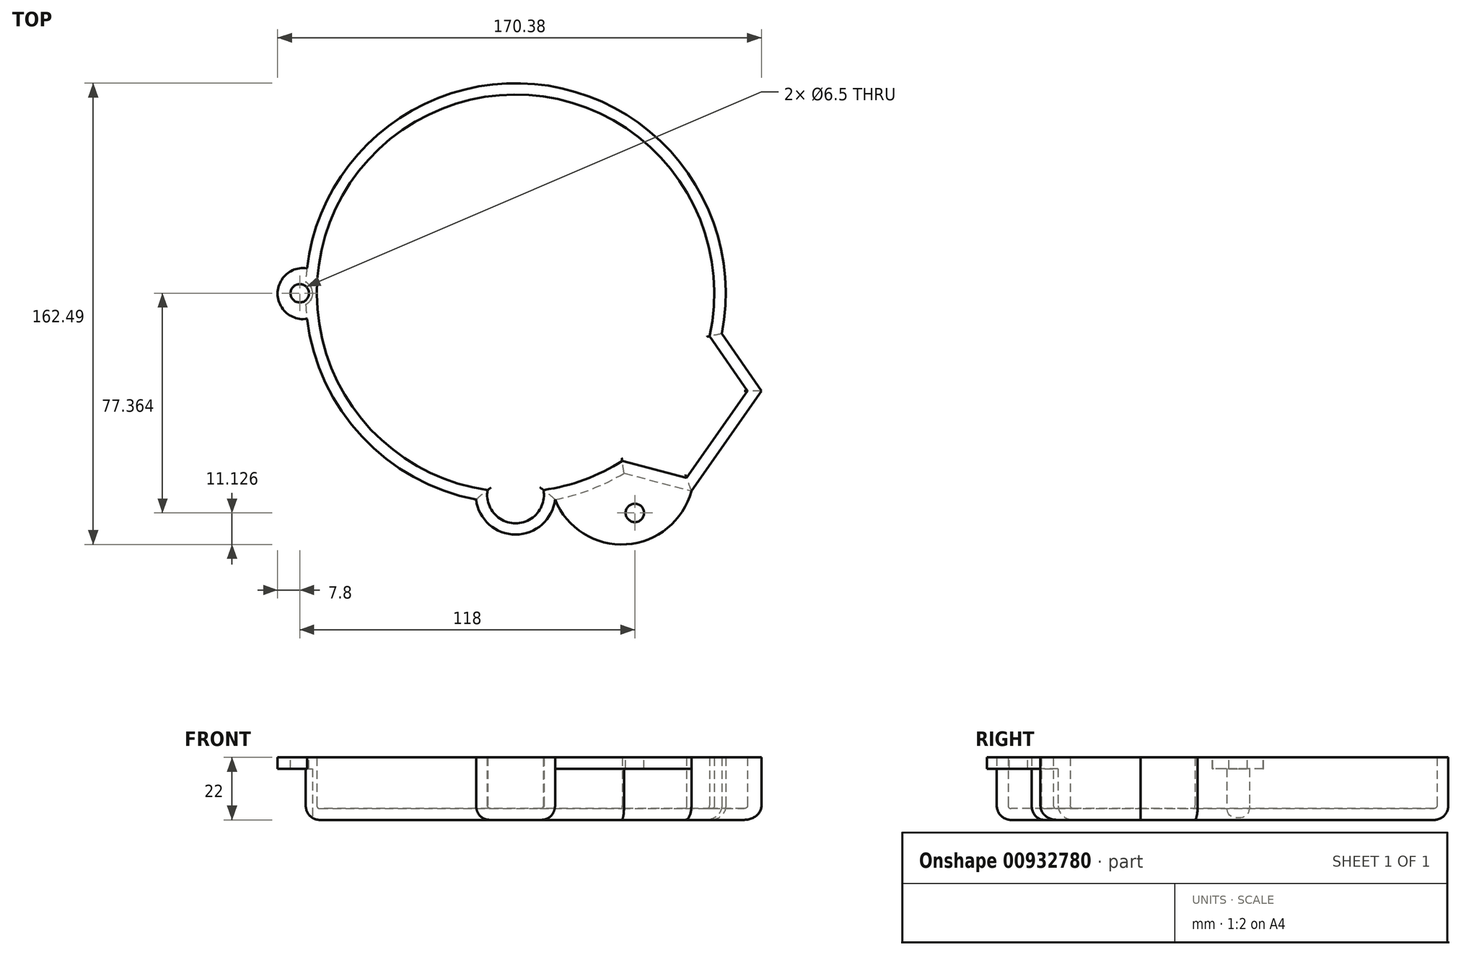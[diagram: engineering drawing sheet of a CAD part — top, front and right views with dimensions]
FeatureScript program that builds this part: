
annotation { "Feature Type Name" : "Feature", "Feature Type Description" : "" }
export const myFeature = defineFeature(function(context is Context, id is Id, definition is map)
    precondition{}
    {
        {
            var Q0;
            Q0=qCreatedBy(makeId("Top.planeOp"),FACE);
            var sketch = newSketch(context, id + "F0", { "sketchPlane" : qUnion([Q0])});
            skCircle(sketch, "E0", {"center": v(0, 0) * mm, "radius": 74 * mm});
            skSolve(sketch);
        }
        {
            var Q0;
            Q0 = qSketchRegion(id + "F0", true);
            extrude(context, id + "F1", {"entities" : qUnion([Q0]), "depth" : 22 * mm, "offsetDistance" : 25 * mm});
        }
        {
            var Q0;
            Q0=makeQuery(id+"F1.opExtrude","CAP_FACE",FACE,{"disambiguationData":[OSD([sQuery(id+"F0.wireOp",EDGE,"E0")])],"isStart":true});
            var sketch = newSketch(context, id + "F2", { "sketchPlane" : qUnion([Q0])});
            skCircle(sketch, "E1", {"center": v(0, 71) * mm, "radius": 14 * mm});
            skSolve(sketch);
        }
        {
            var Q0;
            Q0 = qSketchRegion(id + "F2", true);
            extrude(context, id + "F3", {"entities" : qUnion([Q0]), "operationType" : NewBodyOperationType.ADD, "oppositeDirection" : true, "depth" : 22 * mm, "offsetDistance" : 25 * mm});
        }
        {
            var Q0;
            Q0=makeQuery(id+"F3.boolean.opBoolean","MERGE",FACE,{"derivedFrom":[makeQuery(id+"F1.opExtrude","CAP_FACE",FACE,{"disambiguationData":[OSD([sQuery(id+"F0.wireOp",EDGE,"E0")])],"isStart":true}),makeQuery(id+"F3.opExtrude","CAP_FACE",FACE,{"disambiguationData":[OSD([sQuery(id+"F2.wireOp",EDGE,"E1")])],"isStart":true})]});
            var sketch = newSketch(context, id + "F4", { "sketchPlane" : qUnion([Q0])});
            skLineSegment(sketch, "E2", {"start": v(38.19, 63.38) * mm, "end": v(61.9, 69.62) * mm});
            skLineSegment(sketch, "E3", {"start": v(61.9, 69.62) * mm, "end": v(86.58, 34.4) * mm});
            skLineSegment(sketch, "E4", {"start": v(86.58, 34.4) * mm, "end": v(72.62, 14.24) * mm});
            skLineSegment(sketch, "E5", {"start": v(38.19, 63.38) * mm, "end": v(72.62, 14.24) * mm});
            skSolve(sketch);
        }
        {
            var Q0;
            Q0 = qSketchRegion(id + "F4", true);
            extrude(context, id + "F5", {"entities" : qUnion([Q0]), "operationType" : NewBodyOperationType.ADD, "oppositeDirection" : true, "depth" : 22 * mm, "offsetDistance" : 25 * mm});
        }
        {
            var Q0;
            {var subQ1=sQuery(id+"F0.wireOp",EDGE,"E0");var subQ2=sQuery(id+"F4.wireOp",EDGE,"E2");Q0=makeQuery(id+"F5.boolean.opBoolean","SPLIT",EDGE,{"disambiguationData":[TD([makeQuery(id+"F5.opExtrude","SWEPT_FACE",FACE,{"disambiguationData":[OSD([subQ2])]})])],"derivedFrom":makeQuery(id+"F1.opExtrude","CAP_EDGE",EDGE,{"disambiguationData":[OSD([subQ1])],"isStart":true})});}
            var Q1;
            Q1=makeQuery(id+"F5.opExtrude","CAP_EDGE",EDGE,{"disambiguationData":[OSD([sQuery(id+"F4.wireOp",EDGE,"E2")])],"isStart":true});
            var Q2;
            Q2=makeQuery(id+"F5.opExtrude","CAP_EDGE",EDGE,{"disambiguationData":[OSD([sQuery(id+"F4.wireOp",EDGE,"E3")])],"isStart":true});
            var Q3;
            Q3=makeQuery(id+"F5.opExtrude","CAP_EDGE",EDGE,{"disambiguationData":[OSD([sQuery(id+"F4.wireOp",EDGE,"E4")])],"isStart":true});
            var Q4;
            {var subQ1=sQuery(id+"F0.wireOp",EDGE,"E0");var subQ2=sQuery(id+"F4.wireOp",EDGE,"E4");Q4=makeQuery(id+"F5.boolean.opBoolean","SPLIT",EDGE,{"disambiguationData":[TD([makeQuery(id+"F5.opExtrude","SWEPT_FACE",FACE,{"disambiguationData":[OSD([subQ2])]})])],"derivedFrom":makeQuery(id+"F1.opExtrude","CAP_EDGE",EDGE,{"disambiguationData":[OSD([subQ1])],"isStart":true})});}
            var Q5;
            Q5=makeQuery(id+"F3.opExtrude","CAP_EDGE",EDGE,{"disambiguationData":[OSD([sQuery(id+"F2.wireOp",EDGE,"E1")])],"isStart":true});
            fillet(context, id + "F6", {"entities" : qUnion([Q0, Q1, Q2, Q3, Q4, Q5]), "radius" : 5 * mm, "tangentPropagation" : true, "allowEdgeOverflow" : false});
        }
        {
            var Q0;
            Q0=makeQuery(id+"F5.boolean.opBoolean","MERGE",FACE,{"derivedFrom":[makeQuery(id+"F3.boolean.opBoolean","MERGE",FACE,{"derivedFrom":[makeQuery(id+"F1.opExtrude","CAP_FACE",FACE,{"disambiguationData":[OSD([sQuery(id+"F0.wireOp",EDGE,"E0")])],"isStart":false}),makeQuery(id+"F3.opExtrude","CAP_FACE",FACE,{"disambiguationData":[OSD([sQuery(id+"F2.wireOp",EDGE,"E1")])],"isStart":false})]}),makeQuery(id+"F5.opExtrude","CAP_FACE",FACE,{"disambiguationData":[OSD([sQuery(id+"F4.wireOp",EDGE,"E2"),sQuery(id+"F4.wireOp",EDGE,"E3"),sQuery(id+"F4.wireOp",EDGE,"E4"),sQuery(id+"F4.wireOp",EDGE,"E5")])],"isStart":false})]});
            shell(context, id + "F7", {"entities" : qUnion([Q0]), "thickness" : 4 * mm});
        }
        {
            var Q0;
            Q0=makeQuery(id+"F5.boolean.opBoolean","MERGE",FACE,{"derivedFrom":[makeQuery(id+"F3.boolean.opBoolean","MERGE",FACE,{"derivedFrom":[makeQuery(id+"F1.opExtrude","CAP_FACE",FACE,{"disambiguationData":[OSD([sQuery(id+"F0.wireOp",EDGE,"E0")])],"isStart":false}),makeQuery(id+"F3.opExtrude","CAP_FACE",FACE,{"disambiguationData":[OSD([sQuery(id+"F2.wireOp",EDGE,"E1")])],"isStart":false})]}),makeQuery(id+"F5.opExtrude","CAP_FACE",FACE,{"disambiguationData":[OSD([sQuery(id+"F4.wireOp",EDGE,"E2"),sQuery(id+"F4.wireOp",EDGE,"E3"),sQuery(id+"F4.wireOp",EDGE,"E4"),sQuery(id+"F4.wireOp",EDGE,"E5")])],"isStart":false})]});
            var sketch = newSketch(context, id + "F8", { "sketchPlane" : qUnion([Q0])});
            skCircle(sketch, "E6", {"center": v(42, -77.36) * mm, "radius": 3.25 * mm});
            skArc(sketch, "E7", {"start": v(13.9, -72.68) * mm, "mid": v(39, -88.44) * mm, "end": v(61.9, -69.62) * mm});
            skLineSegment(sketch, "E8", {"start": v(61.9, -69.62) * mm, "end": v(37.39, -63.14) * mm});
            skLineSegment(sketch, "E9", {"start": v(13.9, -72.68) * mm, "end": v(37.39, -63.14) * mm});
            skSolve(sketch);
        }
        {
            var Q0;
            Q0 = qSketchRegion(id + "F8", true);
            extrude(context, id + "F9", {"entities" : qUnion([Q0]), "operationType" : NewBodyOperationType.ADD, "oppositeDirection" : true, "depth" : 4 * mm, "offsetDistance" : 25 * mm});
        }
        {
            var Q0;
            Q0=makeQuery(id+"F9.boolean.opBoolean","MERGE",FACE,{"derivedFrom":[makeQuery(id+"F5.boolean.opBoolean","MERGE",FACE,{"derivedFrom":[makeQuery(id+"F3.boolean.opBoolean","MERGE",FACE,{"derivedFrom":[makeQuery(id+"F1.opExtrude","CAP_FACE",FACE,{"disambiguationData":[OSD([sQuery(id+"F0.wireOp",EDGE,"E0")])],"isStart":false}),makeQuery(id+"F3.opExtrude","CAP_FACE",FACE,{"disambiguationData":[OSD([sQuery(id+"F2.wireOp",EDGE,"E1")])],"isStart":false})]}),makeQuery(id+"F5.opExtrude","CAP_FACE",FACE,{"disambiguationData":[OSD([sQuery(id+"F4.wireOp",EDGE,"E2"),sQuery(id+"F4.wireOp",EDGE,"E3"),sQuery(id+"F4.wireOp",EDGE,"E4"),sQuery(id+"F4.wireOp",EDGE,"E5")])],"isStart":false})]}),makeQuery(id+"F9.opExtrude","CAP_FACE",FACE,{"disambiguationData":[OSD([sQuery(id+"F8.wireOp",EDGE,"E6"),sQuery(id+"F8.wireOp",EDGE,"E7"),sQuery(id+"F8.wireOp",EDGE,"E8"),sQuery(id+"F8.wireOp",EDGE,"E9")])],"isStart":true})]});
            var sketch = newSketch(context, id + "F10", { "sketchPlane" : qUnion([Q0])});
            skCircle(sketch, "E10", {"center": v(-76, 0) * mm, "radius": 3.25 * mm});
            skArc(sketch, "E11", {"start": v(-73.48, 8.8) * mm, "mid": v(-83.8, -0.11) * mm, "end": v(-73.45, -9) * mm});
            skArc(sketch, "E12", {"start": v(-73.45, -9) * mm, "mid": v(-70.9, -0.1) * mm, "end": v(-73.48, 8.8) * mm});
            skSolve(sketch);
        }
        {
            var Q0;
            Q0 = qSketchRegion(id + "F10", true);
            extrude(context, id + "F11", {"entities" : qUnion([Q0]), "operationType" : NewBodyOperationType.ADD, "oppositeDirection" : true, "depth" : 4 * mm, "offsetDistance" : 25 * mm});
        }
        {
            var Q0;
            Q0=makeQuery(id+"F5.boolean.opBoolean","MERGE",FACE,{"derivedFrom":[makeQuery(id+"F3.boolean.opBoolean","MERGE",FACE,{"derivedFrom":[makeQuery(id+"F1.opExtrude","CAP_FACE",FACE,{"disambiguationData":[OSD([sQuery(id+"F0.wireOp",EDGE,"E0")])],"isStart":true}),makeQuery(id+"F3.opExtrude","CAP_FACE",FACE,{"disambiguationData":[OSD([sQuery(id+"F2.wireOp",EDGE,"E1")])],"isStart":true})]}),makeQuery(id+"F5.opExtrude","CAP_FACE",FACE,{"disambiguationData":[OSD([sQuery(id+"F4.wireOp",EDGE,"E2"),sQuery(id+"F4.wireOp",EDGE,"E3"),sQuery(id+"F4.wireOp",EDGE,"E4"),sQuery(id+"F4.wireOp",EDGE,"E5")])],"isStart":true})]});
            var sketch = newSketch(context, id + "F12", { "sketchPlane" : qUnion([Q0])});
            skCircle(sketch, "E13", {"center": v(-76, 0) * mm, "radius": 4.5 * mm});
            skSolve(sketch);
        }
        {
            var Q0;
            Q0 = qSketchRegion(id + "F12", true);
            extrude(context, id + "F13", {"entities" : qUnion([Q0]), "operationType" : NewBodyOperationType.REMOVE, "oppositeDirection" : true, "depth" : 18 * mm, "offsetDistance" : 25 * mm});
        }
        {
            var Q0;
            Q0=makeQuery(id+"F11.boolean.opBoolean","MERGE",FACE,{"derivedFrom":[makeQuery(id+"F9.boolean.opBoolean","MERGE",FACE,{"derivedFrom":[makeQuery(id+"F5.boolean.opBoolean","MERGE",FACE,{"derivedFrom":[makeQuery(id+"F3.boolean.opBoolean","MERGE",FACE,{"derivedFrom":[makeQuery(id+"F1.opExtrude","CAP_FACE",FACE,{"disambiguationData":[OSD([sQuery(id+"F0.wireOp",EDGE,"E0")])],"isStart":false}),makeQuery(id+"F3.opExtrude","CAP_FACE",FACE,{"disambiguationData":[OSD([sQuery(id+"F2.wireOp",EDGE,"E1")])],"isStart":false})]}),makeQuery(id+"F5.opExtrude","CAP_FACE",FACE,{"disambiguationData":[OSD([sQuery(id+"F4.wireOp",EDGE,"E2"),sQuery(id+"F4.wireOp",EDGE,"E3"),sQuery(id+"F4.wireOp",EDGE,"E4"),sQuery(id+"F4.wireOp",EDGE,"E5")])],"isStart":false})]}),makeQuery(id+"F9.opExtrude","CAP_FACE",FACE,{"disambiguationData":[OSD([sQuery(id+"F8.wireOp",EDGE,"E6"),sQuery(id+"F8.wireOp",EDGE,"E7"),sQuery(id+"F8.wireOp",EDGE,"E8"),sQuery(id+"F8.wireOp",EDGE,"E9")])],"isStart":true})]}),makeQuery(id+"F11.opExtrude","CAP_FACE",FACE,{"disambiguationData":[OSD([sQuery(id+"F10.wireOp",EDGE,"E10"),sQuery(id+"F10.wireOp",EDGE,"E11"),sQuery(id+"F10.wireOp",EDGE,"E12")])],"isStart":true})]});
            var sketch = newSketch(context, id + "F14", { "sketchPlane" : qUnion([Q0])});
            skCircle(sketch, "E14", {"center": v(-76, 0) * mm, "radius": 3.25 * mm});
            skSolve(sketch);
        }
        {
            var Q0;
            Q0 = qSketchRegion(id + "F14", true);
            var Q1;
            Q1=makeQuery(id+"F13.boolean.opBoolean","MERGE",FACE,{"derivedFrom":[makeQuery(id+"F11.opExtrude","CAP_FACE",FACE,{"disambiguationData":[OSD([sQuery(id+"F10.wireOp",EDGE,"E10"),sQuery(id+"F10.wireOp",EDGE,"E11"),sQuery(id+"F10.wireOp",EDGE,"E12")])],"isStart":false})],"fromTools":[makeQuery(id+"F13.opExtrude","CAP_FACE",FACE,{"disambiguationData":[OSD([sQuery(id+"F12.wireOp",EDGE,"E13")])],"isStart":false})]});
            extrude(context, id + "F15", {"entities" : qUnion([Q0]), "operationType" : NewBodyOperationType.REMOVE, "endBound" : BoundingType.UP_TO_SURFACE, "oppositeDirection" : true, "depth" : mm, "endBoundEntityFace" : qUnion([Q1]), "offsetDistance" : 25 * mm});
        }
    });
